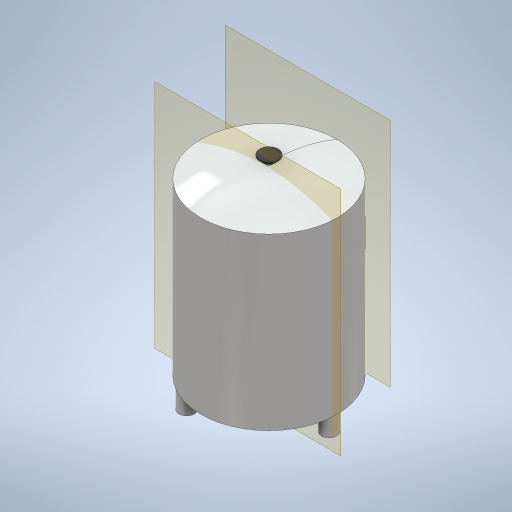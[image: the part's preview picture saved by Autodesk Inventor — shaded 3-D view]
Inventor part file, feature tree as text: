
AUTODESK INVENTOR PART (.ipt)
format: ipt  version: 2024 (Build 280153000, 153)  size: 343,040 bytes
history: native  units: mm
features: sketch x10, extrude x8, plane x4, pattern_circular x1, revolve x1, chamfer x1
ambient origin geometry x8: Origin, YZ Plane, XZ Plane, XY Plane, X Axis, Y Axis, Z Axis, Center Point
bodies: Solid1 (feature_tree)
feature tree (25):
  extrude  "Extrusion1"  Depth=240.0mm
  extrude  "Extrusion2"  Depth=3.0mm TaperAngle=0.0deg
  extrude  "Extrusion3"  Depth=40.0mm TaperAngle=0.0deg
  pattern_circular  "Circular Pattern1"  Count=3 Angle=360.0deg
  revolve  "Revolution1"  Angle=90.0deg
  plane  "Work Plane2"
  sketch  "Sketch5"  dims[d15=15.0mm d16=5.0mm d17=0.0mm]
  extrude  "Extrusion4"  Depth=5.0mm TaperAngle=0.0deg
  extrude  "Extrusion5"  Depth=10.0mm TaperAngle=0.0deg
  chamfer  "Chamfer1"  Distance=7.0mm Angle=45.0deg
  plane  "Work Plane3"
  extrude  "Extrusion6"  Depth=40.0mm
  plane  "Work Plane4"
  extrude  "Extrusion8"  Depth=60.0mm TaperAngle=0.0deg
  plane  "Work Plane5"
  extrude  "Extrusion9"  Depth=60.0mm
  sketch  "Sketch1"  dims[d0=290.0mm d1=240.0mm]
  sketch  "Sketch2"  dims[d2=360.0mm d3=0.0mm d4=3.0mm d5=0.0mm]
  sketch  "Sketch3"  dims[d6=33.0mm d7=40.0mm d8=0.0mm d9=30.0mm d10=360.0deg]
  sketch  "Sketch4"  dims[d13=30.0mm d14=90.0deg]
  sketch  "Sketch6"  dims[d18=40.0mm d19=10.0mm d20=0.0mm d21=7.0mm d22=2.0mm d23=45.0deg]
  sketch  "Sketch7"  dims[d24=40.0mm d25=20.0mm]
  sketch  "Sketch8"  dims[d26=30.0mm d27=0.0mm d31=60.0mm d32=0.0mm]
  sketch  "Sketch11"  dims[d33=80.0mm d34=60.0mm]
  sketch  "Sketch12"  dims[d35=200.0mm d36=40.0mm d37=0.0mm]
